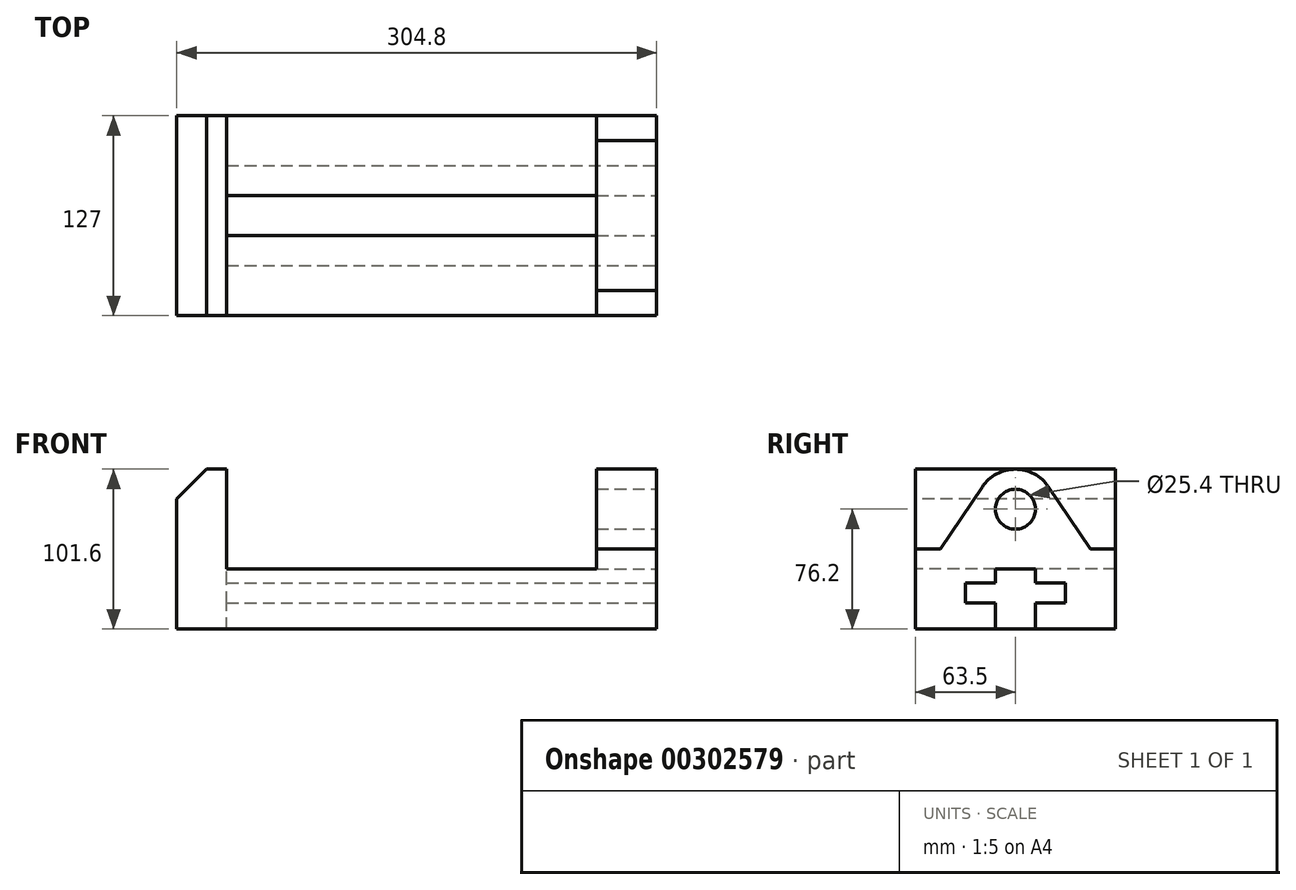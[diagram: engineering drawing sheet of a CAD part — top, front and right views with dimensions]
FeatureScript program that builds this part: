
annotation { "Feature Type Name" : "Feature", "Feature Type Description" : "" }
export const myFeature = defineFeature(function(context is Context, id is Id, definition is map)
    precondition{}
    {
        {
            var Q0;
            Q0=qCreatedBy(makeId("Front.planeOp"),FACE);
            var sketch = newSketch(context, id + "F0", { "sketchPlane" : qUnion([Q0])});
            skLineSegment(sketch, "E0.bottom", {"start": v(0, 0) * mm, "end": v(304.8, 0) * mm});
            skLineSegment(sketch, "E0.top", {"start": v(0, 101.6) * mm, "end": v(304.8, 101.6) * mm});
            skLineSegment(sketch, "E0.left", {"start": v(0, 0) * mm, "end": v(0, 101.6) * mm});
            skLineSegment(sketch, "E0.right", {"start": v(304.8, 0) * mm, "end": v(304.8, 101.6) * mm});
            skSolve(sketch);
        }
        {
            var Q0;
            Q0 = qSketchRegion(id + "F0", true);
            extrude(context, id + "F1", {"entities" : qUnion([Q0]), "depth" : 127 * mm});
        }
        {
            var Q0;
            Q0=makeQuery(id+"F1.opExtrude","CAP_FACE",FACE,{"disambiguationData":[OSD([sQuery(id+"F0.wireOp",EDGE,"E0.bottom"),sQuery(id+"F0.wireOp",EDGE,"E0.top"),sQuery(id+"F0.wireOp",EDGE,"E0.left"),sQuery(id+"F0.wireOp",EDGE,"E0.right")])],"isStart":false});
            var sketch = newSketch(context, id + "F2", { "sketchPlane" : qUnion([Q0])});
            skLineSegment(sketch, "E1", {"start": v(266.7, 101.6) * mm, "end": v(31.75, 101.6) * mm});
            skLineSegment(sketch, "E2", {"start": v(31.75, 101.6) * mm, "end": v(31.75, 38.1) * mm});
            skLineSegment(sketch, "E3", {"start": v(31.75, 38.1) * mm, "end": v(266.7, 38.1) * mm});
            skLineSegment(sketch, "E4", {"start": v(266.7, 38.1) * mm, "end": v(266.7, 101.6) * mm});
            skSolve(sketch);
        }
        {
            var Q0;
            Q0 = qSketchRegion(id + "F2", true);
            extrude(context, id + "F3", {"entities" : qUnion([Q0]), "operationType" : NewBodyOperationType.REMOVE, "endBound" : BoundingType.THROUGH_ALL, "oppositeDirection" : true, "depth" : 25.4 * mm});
        }
        {
            var Q0;
            Q0=makeQuery(id+"F1.opExtrude","CAP_FACE",FACE,{"disambiguationData":[OSD([sQuery(id+"F0.wireOp",EDGE,"E0.bottom"),sQuery(id+"F0.wireOp",EDGE,"E0.top"),sQuery(id+"F0.wireOp",EDGE,"E0.left"),sQuery(id+"F0.wireOp",EDGE,"E0.right")])],"isStart":false});
            var sketch = newSketch(context, id + "F4", { "sketchPlane" : qUnion([Q0])});
            skLineSegment(sketch, "E5", {"start": v(0, 101.6) * mm, "end": v(0, 82.55) * mm});
            skLineSegment(sketch, "E6", {"start": v(0, 101.6) * mm, "end": v(19.05, 101.6) * mm});
            skLineSegment(sketch, "E7", {"start": v(19.05, 101.6) * mm, "end": v(0, 82.55) * mm});
            skSolve(sketch);
        }
        {
            var Q0;
            Q0 = qSketchRegion(id + "F4", true);
            extrude(context, id + "F5", {"entities" : qUnion([Q0]), "operationType" : NewBodyOperationType.REMOVE, "endBound" : BoundingType.THROUGH_ALL, "oppositeDirection" : true, "depth" : 25.4 * mm});
        }
        {
            var Q0;
            Q0=makeQuery(id+"F1.opExtrude","SWEPT_FACE",FACE,{"disambiguationData":[OSD([sQuery(id+"F0.wireOp",EDGE,"E0.right")])]});
            var sketch = newSketch(context, id + "F6", { "sketchPlane" : qUnion([Q0])});
            skLineSegment(sketch, "E8", {"start": v(-127, 0) * mm, "end": v(-127, 50.8) * mm});
            skLineSegment(sketch, "E9", {"start": v(-127, 0) * mm, "end": v(0, 0) * mm});
            skLineSegment(sketch, "E10", {"start": v(0, 0) * mm, "end": v(0, 50.8) * mm});
            skLineSegment(sketch, "E11", {"start": v(-127, 50.8) * mm, "end": v(-111.12, 50.8) * mm});
            skLineSegment(sketch, "E12", {"start": v(0, 50.8) * mm, "end": v(-15.88, 50.8) * mm});
            skLineSegment(sketch, "E13", {"start": v(-63.5, 101.6) * mm, "end": v(-63.5, 0) * mm, "construction": true});
            skLineSegment(sketch, "E14", {"start": v(-63.5, 101.6) * mm, "end": v(-63.5, 123.75) * mm, "construction": true});
            skLineSegment(sketch, "E15", {"start": v(-111.13, 50.8) * mm, "end": v(-84.6, 90.35) * mm});
            skLineSegment(sketch, "E16", {"start": v(-42.4, 90.35) * mm, "end": v(-15.87, 50.8) * mm});
            skPoint(sketch, "E17.visualSharp", {"position": v(-63.5, 121.8) * mm});
            skArc(sketch, "E17.filletArc", {"start": v(-42.4, 90.35) * mm, "mid": v(-63.5, 101.6) * mm, "end": v(-84.6, 90.35) * mm});
            skCircle(sketch, "E18", {"center": v(-63.5, 76.2) * mm, "radius": 12.7 * mm});
            skSolve(sketch);
        }
        {
            var Q0;
            {var subQ4=sQuery(id+"F6.wireOp",EDGE,"E11");Q0=makeQuery(id+"F6.imprint","IMPRINT",FACE,{"disambiguationData":[TD([[makeQuery(id+"F6.imprint","IMPRINT",EDGE,{"derivedFrom":subQ4}),1.0]])]});}
            var Q1;
            {var subQ7=sQuery(id+"F6.wireOp",EDGE,"E12");Q1=makeQuery(id+"F6.imprint","IMPRINT",FACE,{"disambiguationData":[TD([[makeQuery(id+"F6.imprint","IMPRINT",EDGE,{"derivedFrom":subQ7}),-1.0]])]});}
            var Q2;
            Q2=makeQuery(id+"F6.imprint","IMPRINT",FACE,{"disambiguationData":[TD([[makeQuery(id+"F6.imprint","IMPRINT",EDGE,{"derivedFrom":sQuery(id+"F6.wireOp",EDGE,"E18")}),1.0]])]});
            var Q3;
            Q3=makeQuery(id+"F3.boolean.opBoolean","COPY",FACE,{"derivedFrom":makeQuery(id+"F3.opExtrude","SWEPT_FACE",FACE,{"disambiguationData":[OSD([sQuery(id+"F2.wireOp",EDGE,"E4")])]})});
            extrude(context, id + "F7", {"entities" : qUnion([Q0, Q1, Q2]), "operationType" : NewBodyOperationType.REMOVE, "endBound" : BoundingType.UP_TO_SURFACE, "oppositeDirection" : true, "endBoundEntityFace" : qUnion([Q3]), "depth" : 25.4 * mm});
        }
        {
            var Q0;
            Q0=makeQuery(id+"F1.opExtrude","SWEPT_FACE",FACE,{"disambiguationData":[OSD([sQuery(id+"F0.wireOp",EDGE,"E0.right")])]});
            var sketch = newSketch(context, id + "F8", { "sketchPlane" : qUnion([Q0])});
            skLineSegment(sketch, "E19", {"start": v(-63.5, 101.6) * mm, "end": v(-63.5, 0) * mm, "construction": true});
            skLineSegment(sketch, "E20.0", {"start": v(-76.2, 0) * mm, "end": v(-63.5, 0) * mm});
            skLineSegment(sketch, "E21", {"start": v(-76.2, 0) * mm, "end": v(-76.2, 16.5) * mm});
            skLineSegment(sketch, "E22", {"start": v(-76.2, 16.5) * mm, "end": v(-95.25, 16.5) * mm});
            skLineSegment(sketch, "E23", {"start": v(-95.25, 16.5) * mm, "end": v(-95.25, 29.2) * mm});
            skLineSegment(sketch, "E24", {"start": v(-95.25, 29.2) * mm, "end": v(-76.2, 29.2) * mm});
            skLineSegment(sketch, "E25", {"start": v(-76.2, 29.2) * mm, "end": v(-76.2, 38.1) * mm});
            skLineSegment(sketch, "E26", {"start": v(-76.2, 38.1) * mm, "end": v(-63.5, 38.1) * mm});
            skPoint(sketch, "E27.orphan", {"position": v(-127, 0) * mm});
            skPoint(sketch, "E28.orphan", {"position": v(0, 0) * mm});
            skLineSegment(sketch, "E29.MirrorCS", {"start": v(-50.8, 29.2) * mm, "end": v(-50.8, 38.1) * mm});
            skLineSegment(sketch, "E30.MirrorCS", {"start": v(-50.8, 38.1) * mm, "end": v(-63.5, 38.1) * mm});
            skLineSegment(sketch, "E31.MirrorCS", {"start": v(-50.8, 0) * mm, "end": v(-63.5, 0) * mm});
            skLineSegment(sketch, "E32.MirrorCS", {"start": v(-50.8, 0) * mm, "end": v(-50.8, 16.5) * mm});
            skLineSegment(sketch, "E33.MirrorCS", {"start": v(-50.8, 16.5) * mm, "end": v(-31.75, 16.5) * mm});
            skLineSegment(sketch, "E34.MirrorCS", {"start": v(-31.75, 29.2) * mm, "end": v(-50.8, 29.2) * mm});
            skLineSegment(sketch, "E35.MirrorCS", {"start": v(-31.75, 16.5) * mm, "end": v(-31.75, 29.2) * mm});
            skSolve(sketch);
        }
        {
            var Q0;
            Q0 = qSketchRegion(id + "F8", true);
            var Q1;
            Q1=makeQuery(id+"F3.boolean.opBoolean","COPY",FACE,{"derivedFrom":makeQuery(id+"F3.opExtrude","SWEPT_FACE",FACE,{"disambiguationData":[OSD([sQuery(id+"F2.wireOp",EDGE,"E2")])]})});
            extrude(context, id + "F9", {"entities" : qUnion([Q0]), "operationType" : NewBodyOperationType.REMOVE, "endBound" : BoundingType.UP_TO_SURFACE, "oppositeDirection" : true, "endBoundEntityFace" : qUnion([Q1]), "depth" : 25.4 * mm});
        }
    });
